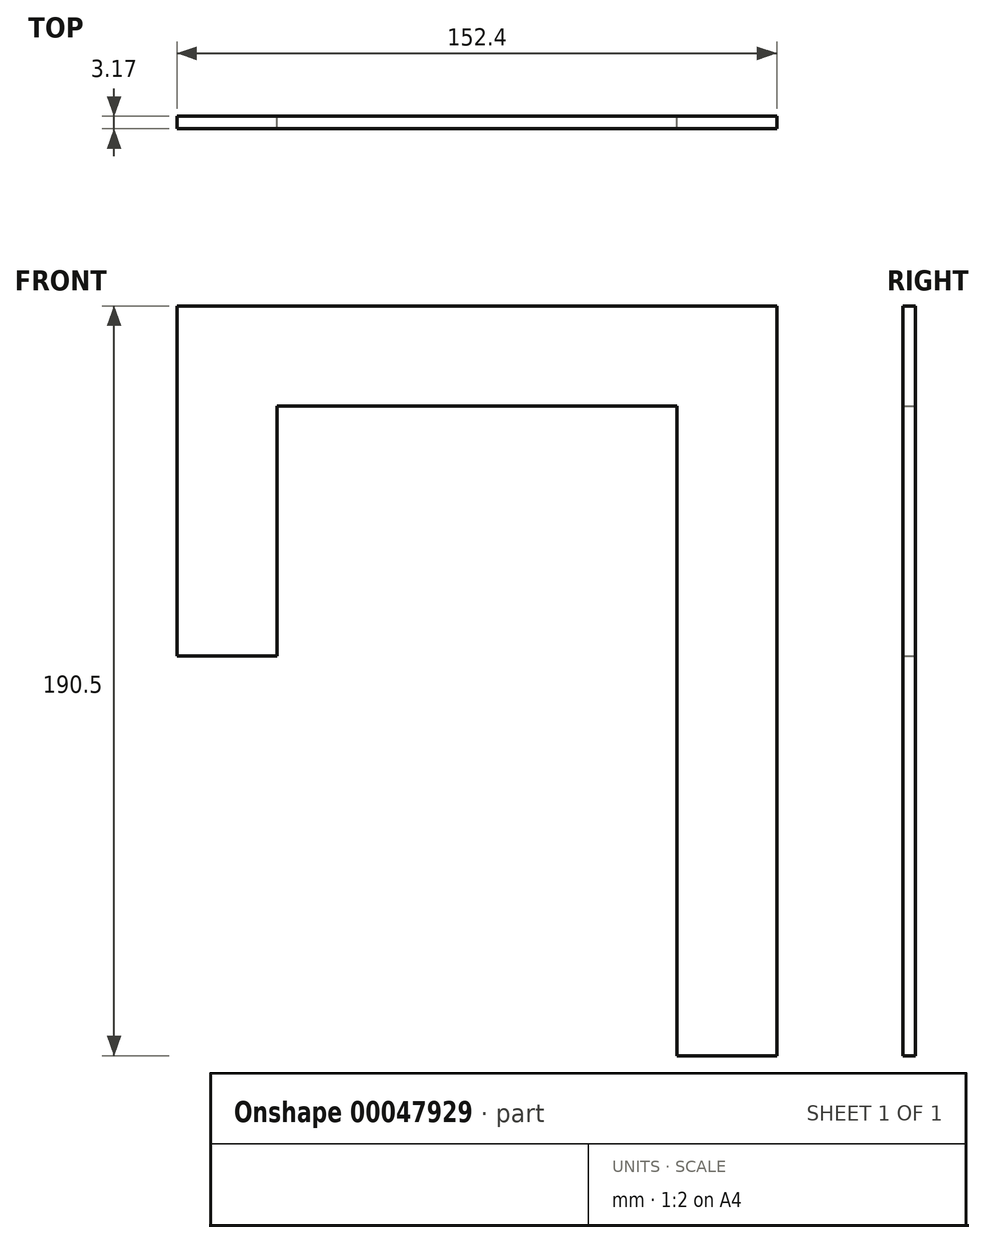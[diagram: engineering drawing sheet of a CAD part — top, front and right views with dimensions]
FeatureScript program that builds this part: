
annotation { "Feature Type Name" : "Feature", "Feature Type Description" : "" }
export const myFeature = defineFeature(function(context is Context, id is Id, definition is map)
    precondition{}
    {
        {
            var Q0;
            Q0=qCreatedBy(makeId("Front.planeOp"),FACE);
            var sketch = newSketch(context, id + "F0", { "sketchPlane" : qUnion([Q0])});
            skLineSegment(sketch, "E0.bottom", {"start": v(-57.46, -49.24) * mm, "end": v(-32.06, -49.24) * mm});
            skLineSegment(sketch, "E0.top", {"start": v(-57.46, 39.66) * mm, "end": v(-32.06, 39.66) * mm});
            skLineSegment(sketch, "E0.left", {"start": v(-57.46, -49.24) * mm, "end": v(-57.46, 39.66) * mm});
            skLineSegment(sketch, "E0.right", {"start": v(-32.06, -49.24) * mm, "end": v(-32.06, 14.26) * mm});
            skLineSegment(sketch, "E1.bottom", {"start": v(-57.46, 39.66) * mm, "end": v(94.94, 39.66) * mm});
            skLineSegment(sketch, "E1.top", {"start": v(-32.06, 14.26) * mm, "end": v(69.54, 14.26) * mm});
            skLineSegment(sketch, "E1.left", {"start": v(-57.46, 39.66) * mm, "end": v(-57.46, 14.26) * mm});
            skLineSegment(sketch, "E1.right", {"start": v(94.94, 39.66) * mm, "end": v(94.94, 14.26) * mm});
            skLineSegment(sketch, "E2.bottom", {"start": v(94.94, 39.66) * mm, "end": v(69.54, 39.66) * mm});
            skLineSegment(sketch, "E2.top", {"start": v(94.94, -150.84) * mm, "end": v(69.54, -150.84) * mm});
            skLineSegment(sketch, "E2.left", {"start": v(94.94, 39.66) * mm, "end": v(94.94, -150.84) * mm});
            skLineSegment(sketch, "E2.right", {"start": v(69.54, 14.26) * mm, "end": v(69.54, -150.84) * mm});
            skSolve(sketch);
        }
        {
            var Q0;
            Q0=makeQuery(id+"F0.imprint","IMPRINT",FACE,{"disambiguationData":[TD([[makeQuery(id+"F0.imprint","IMPRINT",EDGE,{"derivedFrom":sQuery(id+"F0.wireOp",EDGE,"E0.bottom")}),1.0]])]});
            extrude(context, id + "F1", {"entities" : qUnion([Q0]), "depth" : 3.17 * mm});
        }
    });
